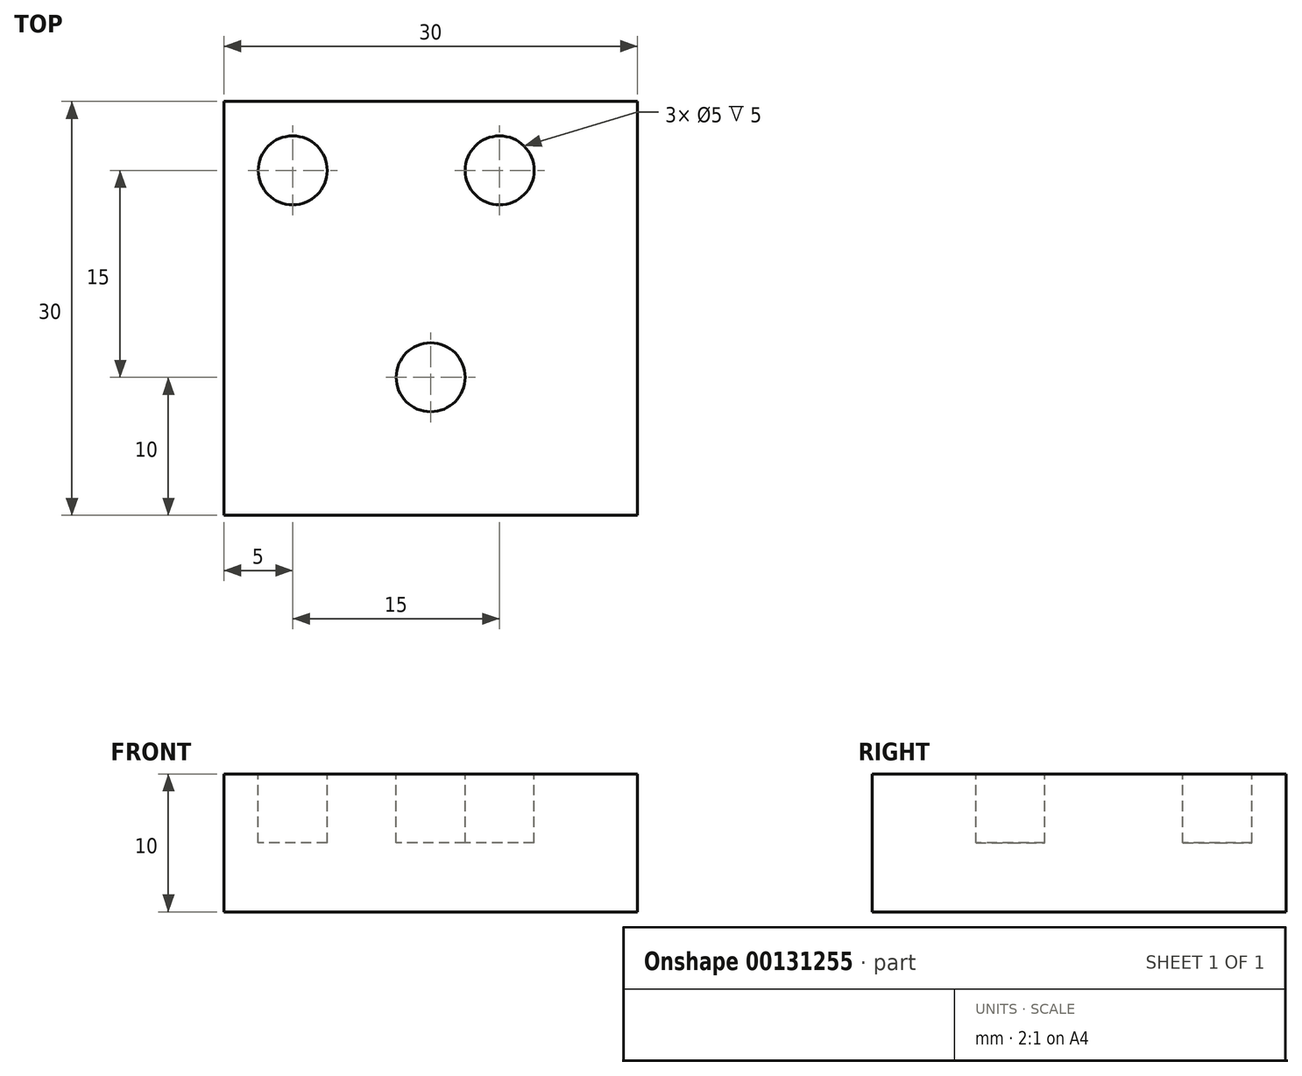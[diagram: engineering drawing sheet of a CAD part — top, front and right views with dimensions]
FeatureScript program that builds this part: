
annotation { "Feature Type Name" : "Feature", "Feature Type Description" : "" }
export const myFeature = defineFeature(function(context is Context, id is Id, definition is map)
    precondition{}
    {
        {
            var Q0;
            Q0=qCreatedBy(makeId("Top.planeOp"),FACE);
            var sketch = newSketch(context, id + "F0", { "sketchPlane" : qUnion([Q0])});
            skLineSegment(sketch, "E0", {"start": v(0, 0) * mm, "end": v(30, 0) * mm});
            skLineSegment(sketch, "E1", {"start": v(30, 0) * mm, "end": v(30, 30) * mm});
            skLineSegment(sketch, "E2", {"start": v(30, 30) * mm, "end": v(0, 30) * mm});
            skLineSegment(sketch, "E3", {"start": v(0, 30) * mm, "end": v(0, 0) * mm});
            skSolve(sketch);
        }
        {
            var Q0;
            Q0=makeQuery(id+"F0.imprint","IMPRINT",FACE,{"disambiguationData":[TD([[makeQuery(id+"F0.imprint","IMPRINT",EDGE,{"derivedFrom":sQuery(id+"F0.wireOp",EDGE,"E0")}),1.0]])]});
            extrude(context, id + "F1", {"entities" : qUnion([Q0]), "depth" : 10 * mm});
        }
        {
            var Q0;
            Q0=makeQuery(id+"F1.opExtrude","CAP_FACE",FACE,{"disambiguationData":[OSD([sQuery(id+"F0.wireOp",EDGE,"E0"),sQuery(id+"F0.wireOp",EDGE,"E1"),sQuery(id+"F0.wireOp",EDGE,"E2"),sQuery(id+"F0.wireOp",EDGE,"E3")])],"isStart":false});
            var sketch = newSketch(context, id + "F2", { "sketchPlane" : qUnion([Q0])});
            skLineSegment(sketch, "E4", {"start": v(10, 30) * mm, "end": v(10, 0) * mm, "construction": true});
            skLineSegment(sketch, "E5", {"start": v(0, 20) * mm, "end": v(30, 20) * mm, "construction": true});
            skLineSegment(sketch, "E6", {"start": v(0, 25) * mm, "end": v(10, 25) * mm, "construction": true});
            skLineSegment(sketch, "E7", {"start": v(5, 30) * mm, "end": v(5, 20) * mm, "construction": true});
            skCircle(sketch, "E8", {"center": v(5, 25) * mm, "radius": 2.5 * mm});
            skLineSegment(sketch, "E9", {"start": v(20, 30) * mm, "end": v(20, 20) * mm, "construction": true});
            skLineSegment(sketch, "E10", {"start": v(10, 25) * mm, "end": v(30, 25) * mm, "construction": true});
            skCircle(sketch, "E11", {"center": v(20, 25) * mm, "radius": 2.5 * mm});
            skLineSegment(sketch, "E12", {"start": v(0, 10) * mm, "end": v(30, 10) * mm, "construction": true});
            skLineSegment(sketch, "E13", {"start": v(15, 10) * mm, "end": v(15, 0) * mm, "construction": true});
            skCircle(sketch, "E14", {"center": v(15, 10) * mm, "radius": 2.5 * mm});
            skSolve(sketch);
        }
        {
            var Q0;
            Q0 = qSketchRegion(id + "F2", true);
            extrude(context, id + "F3", {"entities" : qUnion([Q0]), "operationType" : NewBodyOperationType.REMOVE, "oppositeDirection" : true, "depth" : 5 * mm});
        }
    });
